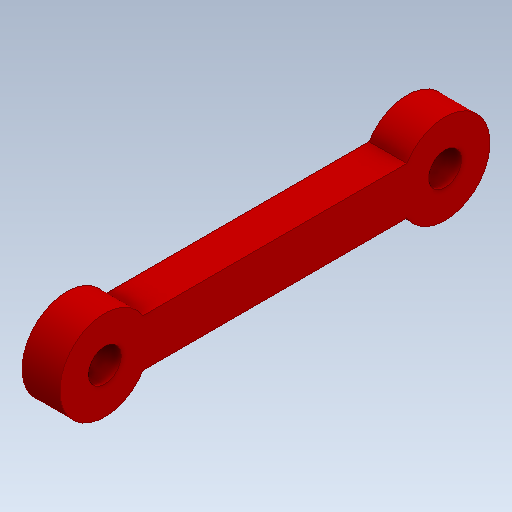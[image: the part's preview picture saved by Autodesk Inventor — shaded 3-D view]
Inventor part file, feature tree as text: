
AUTODESK INVENTOR PART (.ipt)
format: ipt  version: 2020 (Build 240168000, 168)  size: 119,808 bytes
history: native  units: in
note: dims shown in document units (in); Inventor stores cm internally (conversion verified against a paired STEP export)
features: extrude x1, sketch x1
ambient origin geometry x8: Origin, YZ Plane, XZ Plane, XY Plane, X Axis, Y Axis, Z Axis, Center Point
bodies: Solid1 (feature_tree)
feature tree (2):
  extrude  "Extrusion1"  Depth=1.4173in
  sketch  "Sketch1"  dims[d0=0.1378in d1=1.4173in d2=0.1181in d3=0.1181in d4=0.1969in d5=0.1575in d6=0.0in]
